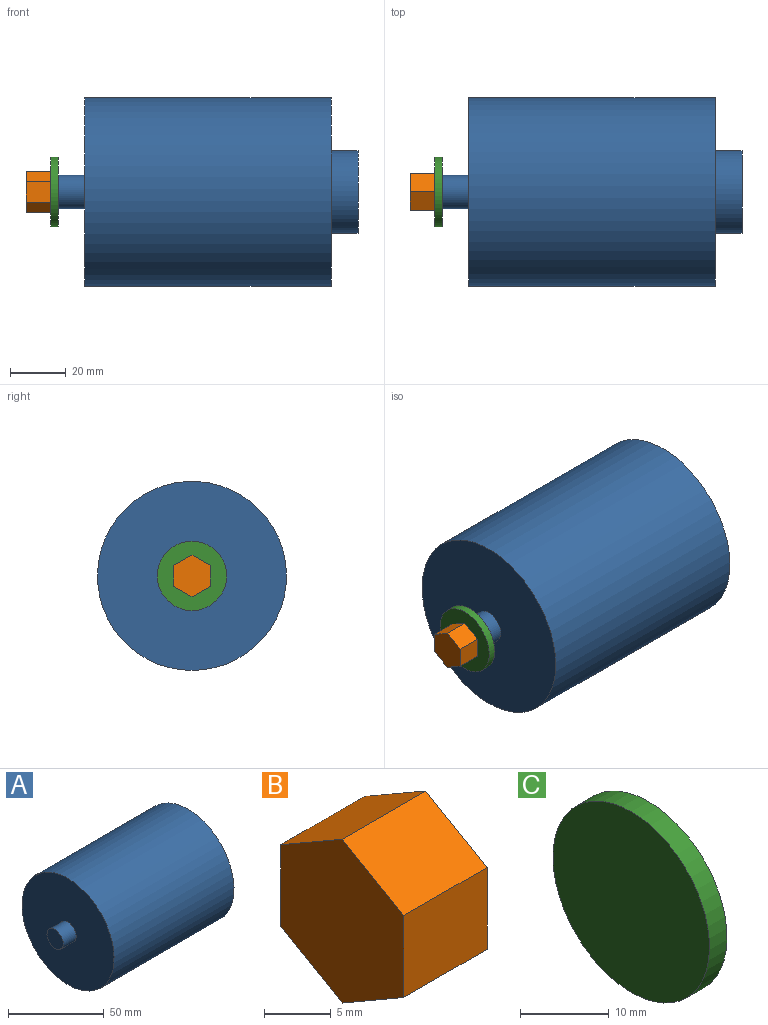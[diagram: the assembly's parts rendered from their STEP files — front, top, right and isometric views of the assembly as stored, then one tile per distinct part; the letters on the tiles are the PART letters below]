
ASSEMBLY  parts=3 mates=2
PART A: 7 faces, bbox 108x68.1x68.1 mm
  f0: cylinder r=34.05mm len=88.7mm, axis (-1,0,0), area 18976.7mm2, adj f1,f2
  f1: plane 68.1x68.1mm, normal (1,0,0), area 2947.2mm2, adj f0,f3
  f2: plane 68.1x68.1mm, normal (-1,0,0), area 3529.3mm2, adj f0,f5
  f3: cylinder r=14.88mm len=29.75mm, axis (-1,0,0), area 906.6mm2, adj f1,f4
  f4: plane 29.75x29.75mm, normal (1,0,0), area 695.1mm2, adj f3
  f5: cylinder r=6mm len=12mm, axis (1,0,0), area 360mm2, adj f2,f6
  f6: plane 12x12mm, normal (-1,0,0), area 113.1mm2, adj f5
PART B: 8 faces, bbox 8.9x13x15 mm
  f0: plane 8.85x6.5mm, normal (0,-0.5,0.87), area 66.4mm2, adj f1,f5,f6,f7
  f1: plane 8.85x6.5mm, normal (0,0.5,0.87), area 66.4mm2, adj f0,f2,f6,f7
  f2: plane 8.85x7.51mm, normal (0,1,0), area 66.4mm2, adj f1,f3,f6,f7
  f3: plane 8.85x6.5mm, normal (0,0.5,-0.87), area 66.4mm2, adj f2,f4,f6,f7
  f4: plane 8.85x6.5mm, normal (0,-0.5,-0.87), area 66.4mm2, adj f3,f5,f6,f7
  f5: plane 8.85x7.51mm, normal (0,-1,0), area 66.4mm2, adj f0,f4,f6,f7
  f6: plane 15.01x13mm, normal (-1,0,0), area 146.4mm2, adj f0,f1,f2,f3,f4,f5
  f7: plane 15.01x13mm, normal (1,0,0), area 146.4mm2, adj f0,f1,f2,f3,f4,f5
PART C: 3 faces, bbox 2.8x25x25 mm
  f0: cylinder r=12.5mm len=25mm, axis (1,0,0), area 219.9mm2, adj f1,f2
  f1: plane 25x25mm, normal (-1,0,0), area 490.9mm2, adj f0
  f2: plane 25x25mm, normal (1,0,0), area 490.9mm2, adj f0
PLACE A at identity
PLACE B at identity
PLACE C at identity
MATE fastened B.f7 <-> C.f0  axis (1,0,0) through (-56.7,0,0)mm
MATE fastened C.f0 <-> A.f5  axis (1,0,0) through (-53.9,0,0)mm
